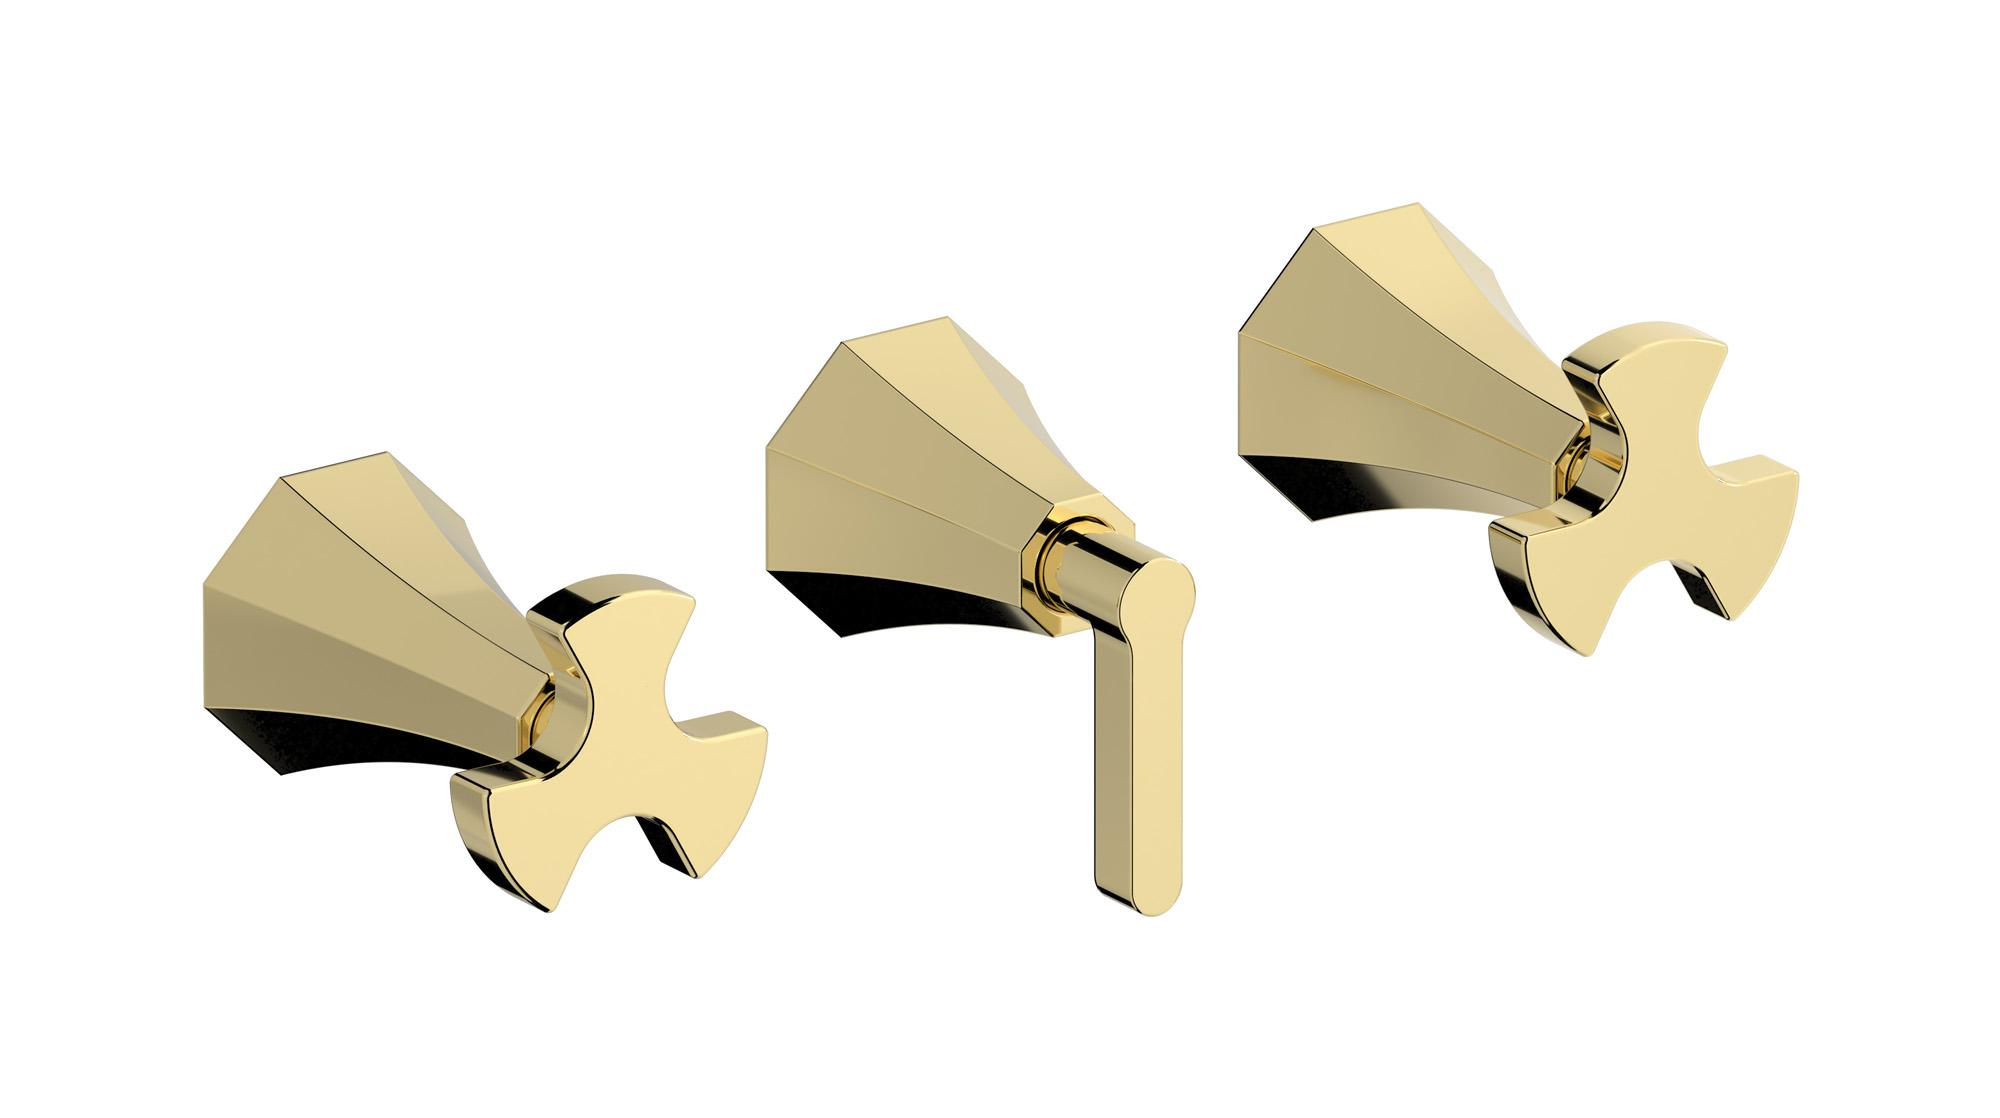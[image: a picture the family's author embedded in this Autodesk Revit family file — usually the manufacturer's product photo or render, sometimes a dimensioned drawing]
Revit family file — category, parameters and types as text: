
# Revit family: BT410
name_source: partatom
category: Apparecchi idraulici
units: mm (PartAtom-declared; Revit-internal decimal feet)

## family parameters
Basato su piano di lavoro = No
Condiviso = No
Mantieni orientamento annotazione = No
Numero OmniClass = 23.45.55.17
Punto di calcolo locali = No
Quota connettore circolare = Usa diametro
Sempre verticale = Sì
Taglio con vuoti quando caricato = No
Tipo di parte = Normale
Titolo OmniClass = Mixing Faucets

## types (7) — shared parameters
Cold water inlet = 10 mm  [stored 0.0328084 ft]
Commenti sul tipo = Shower mixer
Connessione CW = No
Connessione HW = No
Connessione di scarico = No
Connessione di ventilazione = No
Descrizione = Three holes wall mounted shower with two ways diverter
Hot water inlet = 10 mm  [stored 0.0328084 ft]
Produttore = IB Rubinetterie S.p.A.
URL = https://www.weareib.it
zero-valued in all types: Prospetto di default

## per-type parameters (varying)
| type | Finishes surface | Immagine tipo | Modello |
| Chrome | IB_Chrome | BT410CC.jpg | BT410CC |
| Platinum | IB_Platinum | BT410PL.jpg | BT410PL |
| Gold | IB_gold | BT410OO.jpg | BT410OO |
| Rose gold | IB_Rose gold | BT410RS.jpg | BT410RS |
| Pale gold | IB_Pale gold | BT410II.jpg | BT410II |
| Modern Bronze | IB_Modern bronze | BT410MB.jpg | BT410MB |
| Brushed Nickel | IB_Brushed nickel | BT410SS.jpg | BT410SS |

note: [stored X ft] marks values corroborated as IEEE doubles in the binary element streams (Revit-internal decimal feet)
